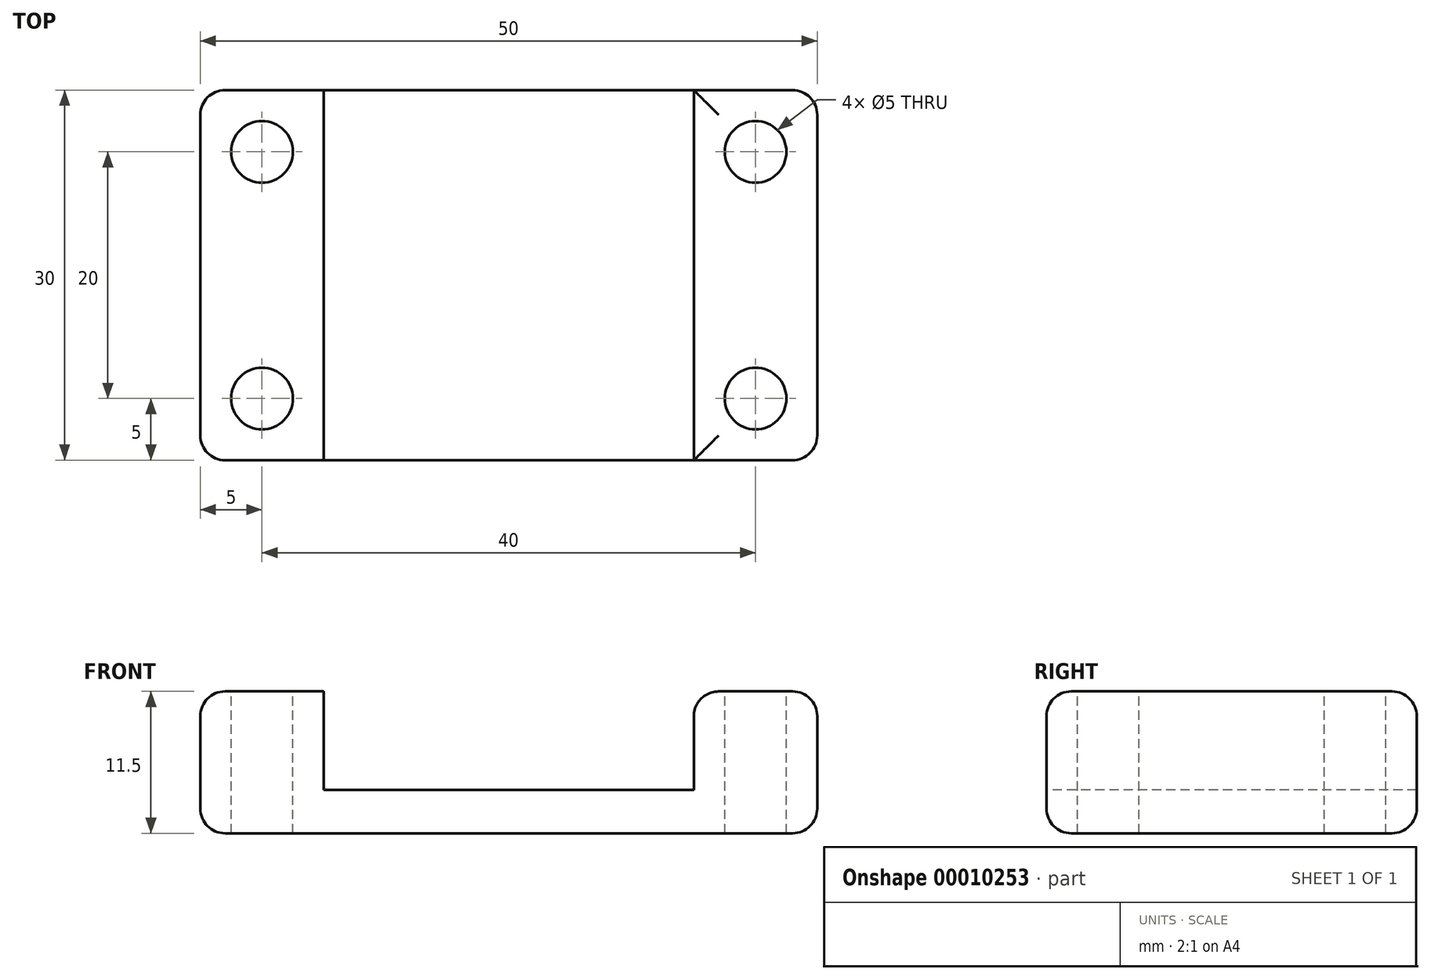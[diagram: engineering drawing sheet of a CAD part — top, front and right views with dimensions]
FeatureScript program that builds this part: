
annotation { "Feature Type Name" : "Feature", "Feature Type Description" : "" }
export const myFeature = defineFeature(function(context is Context, id is Id, definition is map)
    precondition{}
    {
        {
            var Q0;
            Q0=qCreatedBy(makeId("Top.planeOp"),FACE);
            var sketch = newSketch(context, id + "F0", { "sketchPlane" : qUnion([Q0])});
            skLineSegment(sketch, "E0.bottom", {"start": v(-25, 15) * mm, "end": v(25, 15) * mm});
            skLineSegment(sketch, "E0.top", {"start": v(-25, -15) * mm, "end": v(25, -15) * mm});
            skLineSegment(sketch, "E0.left", {"start": v(-25, 15) * mm, "end": v(-25, -15) * mm});
            skLineSegment(sketch, "E0.right", {"start": v(25, 15) * mm, "end": v(25, -15) * mm});
            skSolve(sketch);
        }
        {
            var Q0;
            Q0=makeQuery(id+"F0.imprint","IMPRINT",FACE,{"disambiguationData":[TD([[makeQuery(id+"F0.imprint","IMPRINT",EDGE,{"derivedFrom":sQuery(id+"F0.wireOp",EDGE,"E0.bottom")}),-1.0]])]});
            extrude(context, id + "F1", {"entities" : qUnion([Q0]), "depth" : 11.5 * mm});
        }
        {
            var Q0;
            Q0=makeQuery(id+"F1.opExtrude","CAP_FACE",FACE,{"disambiguationData":[OSD([sQuery(id+"F0.wireOp",EDGE,"E0.bottom"),sQuery(id+"F0.wireOp",EDGE,"E0.top"),sQuery(id+"F0.wireOp",EDGE,"E0.left"),sQuery(id+"F0.wireOp",EDGE,"E0.right")])],"isStart":false});
            var sketch = newSketch(context, id + "F2", { "sketchPlane" : qUnion([Q0])});
            skLineSegment(sketch, "E1.bottom", {"start": v(-15, 15) * mm, "end": v(15, 15) * mm});
            skLineSegment(sketch, "E1.top", {"start": v(-15, -15) * mm, "end": v(15, -15) * mm});
            skLineSegment(sketch, "E1.left", {"start": v(-15, 15) * mm, "end": v(-15, -15) * mm});
            skLineSegment(sketch, "E1.right", {"start": v(15, 15) * mm, "end": v(15, -15) * mm});
            skSolve(sketch);
        }
        {
            var Q0;
            Q0=qSketchRegion(id+"F2",true);
            extrude(context, id + "F3", {"entities" : qUnion([Q0]), "operationType" : NewBodyOperationType.REMOVE, "oppositeDirection" : true, "depth" : 8 * mm});
        }
        {
            var Q0;
            {var subQ0=sQuery(id+"F0.wireOp",EDGE,"E0.bottom");var subQ1=sQuery(id+"F0.wireOp",EDGE,"E0.top");var subQ2=sQuery(id+"F0.wireOp",EDGE,"E0.left");Q0=makeQuery(id+"F3.boolean.opBoolean","SPLIT",FACE,{"disambiguationData":[TD([makeQuery(id+"F1.opExtrude","SWEPT_FACE",FACE,{"disambiguationData":[OSD([subQ2])]})])],"derivedFrom":makeQuery(id+"F1.opExtrude","CAP_FACE",FACE,{"disambiguationData":[OSD([subQ0,subQ1,subQ2,sQuery(id+"F0.wireOp",EDGE,"E0.right")])],"isStart":false})});}
            var sketch = newSketch(context, id + "F4", { "sketchPlane" : qUnion([Q0])});
            skCircle(sketch, "E2", {"center": v(-20, 10) * mm, "radius": 2.5 * mm});
            skCircle(sketch, "E3", {"center": v(-20, -10) * mm, "radius": 2.5 * mm});
            skCircle(sketch, "E4", {"center": v(20, 10) * mm, "radius": 2.5 * mm});
            skCircle(sketch, "E5", {"center": v(20, -10) * mm, "radius": 2.5 * mm});
            skSolve(sketch);
        }
        {
            var Q0;
            Q0=qSketchRegion(id+"F4",true);
            extrude(context, id + "F5", {"entities" : qUnion([Q0]), "operationType" : NewBodyOperationType.REMOVE, "endBound" : BoundingType.UP_TO_NEXT, "oppositeDirection" : true, "depth" : 25 * mm});
        }
        {
            var Q0;
            Q0=makeQuery(id+"F1.opExtrude","CAP_EDGE",EDGE,{"disambiguationData":[OSD([sQuery(id+"F0.wireOp",EDGE,"E0.right")])],"isStart":false});
            var Q1;
            {var subQ0=sQuery(id+"F0.wireOp",EDGE,"E0.top");var subQ1=sQuery(id+"F0.wireOp",EDGE,"E0.right");Q1=makeQuery(id+"F3.boolean.opBoolean","SPLIT",EDGE,{"disambiguationData":[TD([makeQuery(id+"F1.opExtrude","SWEPT_FACE",FACE,{"disambiguationData":[OSD([subQ1])]})])],"derivedFrom":makeQuery(id+"F1.opExtrude","CAP_EDGE",EDGE,{"disambiguationData":[OSD([subQ0])],"isStart":false})});}
            var Q2;
            {var subQ0=sQuery(id+"F0.wireOp",EDGE,"E0.bottom");var subQ1=sQuery(id+"F0.wireOp",EDGE,"E0.right");Q2=makeQuery(id+"F3.boolean.opBoolean","SPLIT",EDGE,{"disambiguationData":[TD([makeQuery(id+"F1.opExtrude","SWEPT_FACE",FACE,{"disambiguationData":[OSD([subQ1])]})])],"derivedFrom":makeQuery(id+"F1.opExtrude","CAP_EDGE",EDGE,{"disambiguationData":[OSD([subQ0])],"isStart":false})});}
            var Q3;
            {var subQ0=sQuery(id+"F0.wireOp",EDGE,"E0.bottom");var subQ1=sQuery(id+"F0.wireOp",EDGE,"E0.left");Q3=makeQuery(id+"F3.boolean.opBoolean","SPLIT",EDGE,{"disambiguationData":[TD([makeQuery(id+"F1.opExtrude","SWEPT_FACE",FACE,{"disambiguationData":[OSD([subQ1])]})])],"derivedFrom":makeQuery(id+"F1.opExtrude","CAP_EDGE",EDGE,{"disambiguationData":[OSD([subQ0])],"isStart":false})});}
            var Q4;
            {var subQ0=sQuery(id+"F0.wireOp",EDGE,"E0.top");var subQ1=sQuery(id+"F0.wireOp",EDGE,"E0.left");Q4=makeQuery(id+"F3.boolean.opBoolean","SPLIT",EDGE,{"disambiguationData":[TD([makeQuery(id+"F1.opExtrude","SWEPT_FACE",FACE,{"disambiguationData":[OSD([subQ1])]})])],"derivedFrom":makeQuery(id+"F1.opExtrude","CAP_EDGE",EDGE,{"disambiguationData":[OSD([subQ0])],"isStart":false})});}
            var Q5;
            Q5=makeQuery(id+"F3.boolean.opBoolean","COPY",EDGE,{"derivedFrom":makeQuery(id+"F3.opExtrude","CAP_EDGE",EDGE,{"disambiguationData":[OSD([sQuery(id+"F2.wireOp",EDGE,"E1.bottom")])],"isStart":false})});
            var Q6;
            Q6=makeQuery(id+"F3.boolean.opBoolean","COPY",EDGE,{"derivedFrom":makeQuery(id+"F3.opExtrude","SWEPT_EDGE",EDGE,{"disambiguationData":[OSD([sQuery(id+"F0.wireOp",EDGE,"E0.top"),sQuery(id+"F2.wireOp",EDGE,"E1.top"),sQuery(id+"F2.wireOp",EDGE,"E1.left")])]})});
            var Q7;
            Q7=makeQuery(id+"F3.boolean.opBoolean","COPY",EDGE,{"derivedFrom":makeQuery(id+"F3.opExtrude","SWEPT_EDGE",EDGE,{"disambiguationData":[OSD([sQuery(id+"F0.wireOp",EDGE,"E0.bottom"),sQuery(id+"F2.wireOp",EDGE,"E1.bottom"),sQuery(id+"F2.wireOp",EDGE,"E1.left")])]})});
            var Q8;
            Q8=makeQuery(id+"F1.opExtrude","SWEPT_EDGE",EDGE,{"disambiguationData":[OSD([sQuery(id+"F0.wireOp",EDGE,"E0.top"),sQuery(id+"F0.wireOp",EDGE,"E0.left")])]});
            var Q9;
            Q9=makeQuery(id+"F1.opExtrude","CAP_EDGE",EDGE,{"disambiguationData":[OSD([sQuery(id+"F0.wireOp",EDGE,"E0.top")])],"isStart":true});
            var Q10;
            Q10=makeQuery(id+"F1.opExtrude","SWEPT_EDGE",EDGE,{"disambiguationData":[OSD([sQuery(id+"F0.wireOp",EDGE,"E0.bottom"),sQuery(id+"F0.wireOp",EDGE,"E0.left")])]});
            var Q11;
            Q11=makeQuery(id+"F1.opExtrude","CAP_EDGE",EDGE,{"disambiguationData":[OSD([sQuery(id+"F0.wireOp",EDGE,"E0.left")])],"isStart":true});
            var Q12;
            Q12=makeQuery(id+"F3.boolean.opBoolean","COPY",EDGE,{"derivedFrom":makeQuery(id+"F3.opExtrude","CAP_EDGE",EDGE,{"disambiguationData":[OSD([sQuery(id+"F2.wireOp",EDGE,"E1.top")])],"isStart":false})});
            var Q13;
            Q13=makeQuery(id+"F3.boolean.opBoolean","COPY",EDGE,{"derivedFrom":makeQuery(id+"F3.opExtrude","CAP_EDGE",EDGE,{"disambiguationData":[OSD([sQuery(id+"F2.wireOp",EDGE,"E1.right")])],"isStart":true})});
            var Q14;
            Q14=makeQuery(id+"F3.boolean.opBoolean","COPY",EDGE,{"derivedFrom":makeQuery(id+"F3.opExtrude","CAP_EDGE",EDGE,{"disambiguationData":[OSD([sQuery(id+"F2.wireOp",EDGE,"E1.left")])],"isStart":true})});
            var Q15;
            Q15=makeQuery(id+"F1.opExtrude","CAP_EDGE",EDGE,{"disambiguationData":[OSD([sQuery(id+"F0.wireOp",EDGE,"E0.left")])],"isStart":false});
            var Q16;
            Q16=makeQuery(id+"F1.opExtrude","SWEPT_EDGE",EDGE,{"disambiguationData":[OSD([sQuery(id+"F0.wireOp",EDGE,"E0.top"),sQuery(id+"F0.wireOp",EDGE,"E0.right")])]});
            var Q17;
            Q17=makeQuery(id+"F3.boolean.opBoolean","COPY",EDGE,{"derivedFrom":makeQuery(id+"F3.opExtrude","SWEPT_EDGE",EDGE,{"disambiguationData":[OSD([sQuery(id+"F0.wireOp",EDGE,"E0.top"),sQuery(id+"F2.wireOp",EDGE,"E1.top"),sQuery(id+"F2.wireOp",EDGE,"E1.right")])]})});
            var Q18;
            Q18=makeQuery(id+"F3.boolean.opBoolean","COPY",EDGE,{"derivedFrom":makeQuery(id+"F3.opExtrude","SWEPT_EDGE",EDGE,{"disambiguationData":[OSD([sQuery(id+"F0.wireOp",EDGE,"E0.bottom"),sQuery(id+"F2.wireOp",EDGE,"E1.bottom"),sQuery(id+"F2.wireOp",EDGE,"E1.right")])]})});
            var Q19;
            Q19=makeQuery(id+"F1.opExtrude","SWEPT_EDGE",EDGE,{"disambiguationData":[OSD([sQuery(id+"F0.wireOp",EDGE,"E0.bottom"),sQuery(id+"F0.wireOp",EDGE,"E0.right")])]});
            var Q20;
            Q20=makeQuery(id+"F1.opExtrude","CAP_EDGE",EDGE,{"disambiguationData":[OSD([sQuery(id+"F0.wireOp",EDGE,"E0.bottom")])],"isStart":true});
            var Q21;
            Q21=makeQuery(id+"F1.opExtrude","CAP_EDGE",EDGE,{"disambiguationData":[OSD([sQuery(id+"F0.wireOp",EDGE,"E0.right")])],"isStart":true});
            fillet(context, id + "F6", {"entities" : qUnion([Q0, Q1, Q2, Q3, Q4, Q5, Q6, Q7, Q8, Q9, Q10, Q11, Q12, Q13, Q14, Q15, Q16, Q17, Q18, Q19, Q20, Q21]), "radius" : 2 * mm, "tangentPropagation" : true, "allowEdgeOverflow" : false});
        }
    });
